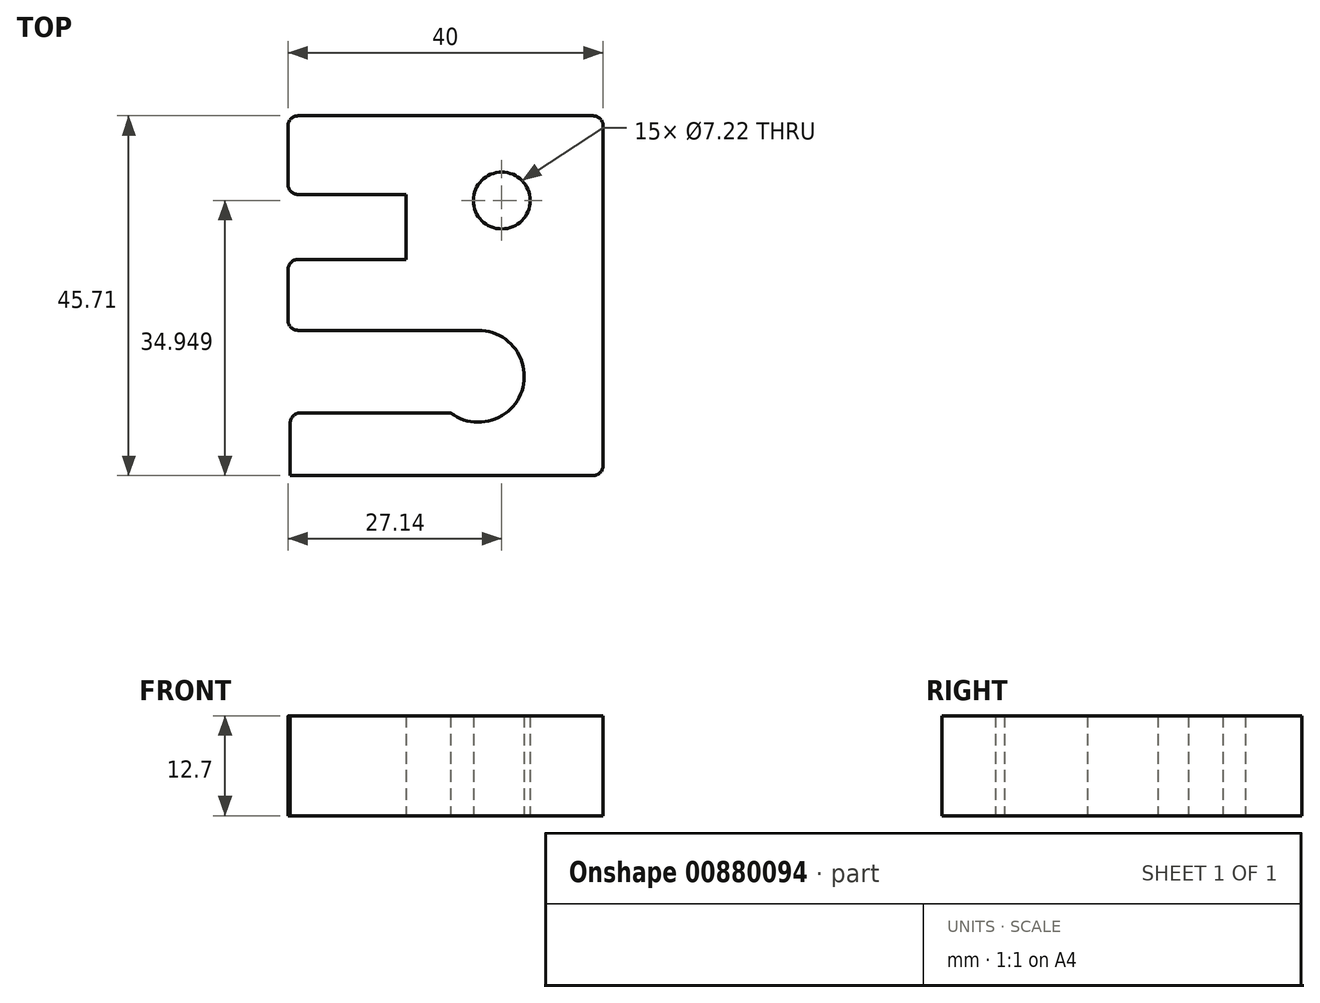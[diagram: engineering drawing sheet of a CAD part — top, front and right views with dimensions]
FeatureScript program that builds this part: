
annotation { "Feature Type Name" : "Feature", "Feature Type Description" : "" }
export const myFeature = defineFeature(function(context is Context, id is Id, definition is map)
    precondition{}
    {
        {
            var Q0;
            Q0=qCreatedBy(makeId("Top.planeOp"),FACE);
            var sketch = newSketch(context, id + "F0", { "sketchPlane" : qUnion([Q0])});
            skLineSegment(sketch, "E0", {"start": v(-25.87, 27.25) * mm, "end": v(11.59, 27.25) * mm});
            skLineSegment(sketch, "E1", {"start": v(12.86, 25.98) * mm, "end": v(12.86, -17.2) * mm});
            skLineSegment(sketch, "E2", {"start": v(11.59, -18.46) * mm, "end": v(-26.87, -18.46) * mm});
            skLineSegment(sketch, "E3", {"start": v(-26.87, -18.46) * mm, "end": v(-26.87, -11.77) * mm});
            skLineSegment(sketch, "E4", {"start": v(-27.14, 25.98) * mm, "end": v(-27.14, 18.52) * mm});
            skLineSegment(sketch, "E5", {"start": v(-25.87, 17.25) * mm, "end": v(-12.14, 17.25) * mm});
            skLineSegment(sketch, "E6", {"start": v(-12.14, 17.25) * mm, "end": v(-12.14, 9) * mm});
            skLineSegment(sketch, "E7", {"start": v(-12.14, 9) * mm, "end": v(-25.87, 9) * mm});
            skLineSegment(sketch, "E8", {"start": v(-27.14, 7.73) * mm, "end": v(-27.14, 1.27) * mm});
            skLineSegment(sketch, "E9", {"start": v(-25.87, 0) * mm, "end": v(-2.98, 0) * mm});
            skLineSegment(sketch, "E10", {"start": v(-25.6, -10.5) * mm, "end": v(-6.48, -10.5) * mm});
            skArc(sketch, "E11", {"start": v(-6.48, -10.5) * mm, "mid": v(2.56, -7.68) * mm, "end": v(-2.98, 0) * mm});
            skCircle(sketch, "E12", {"center": v(0, 16.49) * mm, "radius": 3.61 * mm});
            skPoint(sketch, "E13.visualSharp", {"position": v(-27.14, 17.25) * mm});
            skArc(sketch, "E13.filletArc", {"start": v(-27.14, 18.52) * mm, "mid": v(-26.77, 17.62) * mm, "end": v(-25.87, 17.25) * mm});
            skPoint(sketch, "E14.visualSharp", {"position": v(-27.14, 9) * mm});
            skArc(sketch, "E14.filletArc", {"start": v(-25.87, 9) * mm, "mid": v(-26.77, 8.63) * mm, "end": v(-27.14, 7.73) * mm});
            skPoint(sketch, "E15.visualSharp", {"position": v(-27.14, 0) * mm});
            skArc(sketch, "E15.filletArc", {"start": v(-27.14, 1.27) * mm, "mid": v(-26.77, 0.37) * mm, "end": v(-25.87, 0) * mm});
            skPoint(sketch, "E16.visualSharp", {"position": v(-26.87, -10.5) * mm});
            skArc(sketch, "E16.filletArc", {"start": v(-25.6, -10.5) * mm, "mid": v(-26.5, -10.87) * mm, "end": v(-26.87, -11.77) * mm});
            skPoint(sketch, "E17.visualSharp", {"position": v(-27.14, 27.25) * mm});
            skArc(sketch, "E17.filletArc", {"start": v(-25.87, 27.25) * mm, "mid": v(-26.77, 26.88) * mm, "end": v(-27.14, 25.98) * mm});
            skPoint(sketch, "E18.visualSharp", {"position": v(12.86, 27.25) * mm});
            skArc(sketch, "E18.filletArc", {"start": v(12.86, 25.98) * mm, "mid": v(12.49, 26.88) * mm, "end": v(11.59, 27.25) * mm});
            skPoint(sketch, "E19.visualSharp", {"position": v(12.86, -18.46) * mm});
            skArc(sketch, "E19.filletArc", {"start": v(11.59, -18.46) * mm, "mid": v(12.49, -18.1) * mm, "end": v(12.86, -17.2) * mm});
            skSolve(sketch);
        }
        {
            var Q0;
            Q0=makeQuery(id+"F0.imprint","IMPRINT",FACE,{"disambiguationData":[TD([[makeQuery(id+"F0.imprint","IMPRINT",EDGE,{"derivedFrom":sQuery(id+"F0.wireOp",EDGE,"E0")}),-1.0]])]});
            extrude(context, id + "F1", {"entities" : qUnion([Q0]), "depth" : 12.7 * mm, "offsetDistance" : 25.4 * mm});
        }
    });
